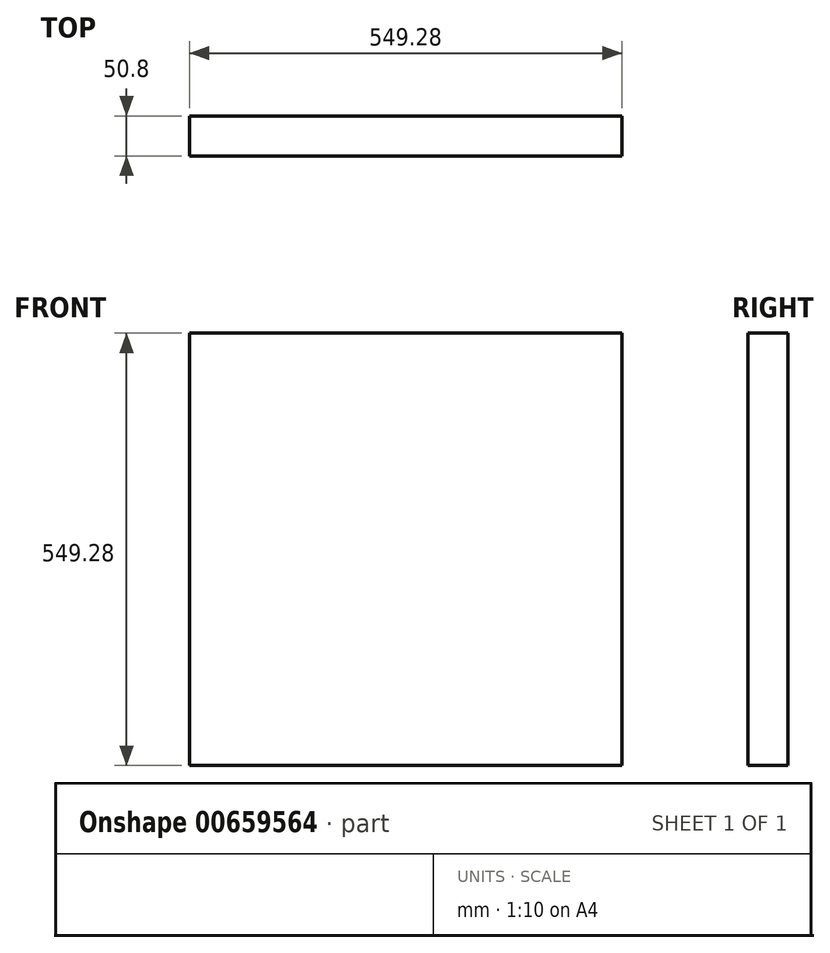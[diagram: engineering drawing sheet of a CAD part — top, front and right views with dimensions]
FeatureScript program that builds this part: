
annotation { "Feature Type Name" : "Feature", "Feature Type Description" : "" }
export const myFeature = defineFeature(function(context is Context, id is Id, definition is map)
    precondition{}
    {
        {
            var Q0;
            Q0=qCreatedBy(makeId("Front.planeOp"),FACE);
            var sketch = newSketch(context, id + "F0", { "sketchPlane" : qUnion([Q0])});
            skLineSegment(sketch, "E0.bottom", {"start": v(274.64, 274.64) * mm, "end": v(-274.64, 274.64) * mm});
            skLineSegment(sketch, "E0.top", {"start": v(274.64, -274.64) * mm, "end": v(-274.64, -274.64) * mm});
            skLineSegment(sketch, "E0.left", {"start": v(274.64, 274.64) * mm, "end": v(274.64, -274.64) * mm});
            skLineSegment(sketch, "E0.right", {"start": v(-274.64, 274.64) * mm, "end": v(-274.64, -274.64) * mm});
            skPoint(sketch, "E0.middle", {"position": v(0, 0) * mm});
            skLineSegment(sketch, "E1", {"start": v(-274.64, 274.64) * mm, "end": v(-273.37, 274.64) * mm, "construction": true});
            skLineSegment(sketch, "E2", {"start": v(-273.37, 274.64) * mm, "end": v(-273.37, 273.37) * mm, "construction": true});
            skPoint(sketch, "E3", {"position": v(-273.37, 273.37) * mm});
            skLineSegment(sketch, "E4.bottom", {"start": v(-273.37, 273.37) * mm, "end": v(-209.87, 273.37) * mm});
            skLineSegment(sketch, "E4.top", {"start": v(-273.37, 209.87) * mm, "end": v(-209.87, 209.87) * mm});
            skLineSegment(sketch, "E4.left", {"start": v(-273.37, 273.37) * mm, "end": v(-273.37, 209.87) * mm});
            skLineSegment(sketch, "E4.right", {"start": v(-209.87, 273.37) * mm, "end": v(-209.87, 209.87) * mm});
            skLineSegment(sketch, "E5", {"start": v(0, 0) * mm, "end": v(0, 20.48) * mm});
            skLineSegment(sketch, "E6", {"start": v(0, 20.48) * mm, "end": v(0, 0) * mm});
            skLineSegment(sketch, "E7", {"start": v(28.9, 0) * mm, "end": v(0, 0) * mm});
            skLineSegment(sketch, "E8.MirrorCS", {"start": v(209.87, 273.37) * mm, "end": v(209.87, 209.87) * mm});
            skLineSegment(sketch, "E9.MirrorCS", {"start": v(273.37, 209.87) * mm, "end": v(209.87, 209.87) * mm});
            skLineSegment(sketch, "E10.MirrorCS", {"start": v(273.37, 273.37) * mm, "end": v(273.37, 209.87) * mm});
            skLineSegment(sketch, "E11.MirrorCS", {"start": v(273.37, 273.37) * mm, "end": v(209.87, 273.37) * mm});
            skLineSegment(sketch, "E12.MirrorCS", {"start": v(-209.87, -273.37) * mm, "end": v(-209.87, -209.87) * mm});
            skLineSegment(sketch, "E13.MirrorCS", {"start": v(-273.37, -209.87) * mm, "end": v(-209.87, -209.87) * mm});
            skLineSegment(sketch, "E14.MirrorCS", {"start": v(-273.37, -273.37) * mm, "end": v(-273.37, -209.87) * mm});
            skLineSegment(sketch, "E15.MirrorCS", {"start": v(-273.37, -273.37) * mm, "end": v(-209.87, -273.37) * mm});
            skLineSegment(sketch, "E16.MirrorCS", {"start": v(273.37, -209.87) * mm, "end": v(209.87, -209.87) * mm});
            skLineSegment(sketch, "E17.MirrorCS", {"start": v(209.87, -273.37) * mm, "end": v(209.87, -209.87) * mm});
            skLineSegment(sketch, "E18.MirrorCS", {"start": v(273.37, -273.37) * mm, "end": v(273.37, -209.87) * mm});
            skLineSegment(sketch, "E19.MirrorCS", {"start": v(273.37, -273.37) * mm, "end": v(209.87, -273.37) * mm});
            skSolve(sketch);
        }
        {
            var Q0;
            Q0=makeQuery(id+"F0.imprint","IMPRINT",FACE,{"disambiguationData":[TD([[makeQuery(id+"F0.imprint","IMPRINT",EDGE,{"derivedFrom":sQuery(id+"F0.wireOp",EDGE,"E0.bottom")}),1.0]])]});
            var Q1;
            Q1=makeQuery(id+"F0.imprint","IMPRINT",FACE,{"disambiguationData":[TD([[makeQuery(id+"F0.imprint","IMPRINT",EDGE,{"derivedFrom":sQuery(id+"F0.wireOp",EDGE,"E8.MirrorCS")}),1.0]])]});
            var Q2;
            Q2=makeQuery(id+"F0.imprint","IMPRINT",FACE,{"disambiguationData":[TD([[makeQuery(id+"F0.imprint","IMPRINT",EDGE,{"derivedFrom":sQuery(id+"F0.wireOp",EDGE,"E4.bottom")}),-1.0]])]});
            var Q3;
            Q3=makeQuery(id+"F0.imprint","IMPRINT",FACE,{"disambiguationData":[TD([[makeQuery(id+"F0.imprint","IMPRINT",EDGE,{"derivedFrom":sQuery(id+"F0.wireOp",EDGE,"E12.MirrorCS")}),1.0]])]});
            var Q4;
            Q4=makeQuery(id+"F0.imprint","IMPRINT",FACE,{"disambiguationData":[TD([[makeQuery(id+"F0.imprint","IMPRINT",EDGE,{"derivedFrom":sQuery(id+"F0.wireOp",EDGE,"E16.MirrorCS")}),1.0]])]});
            extrude(context, id + "F1", {"entities" : qUnion([Q0, Q1, Q2, Q3, Q4]), "depth" : 50.8 * mm});
        }
    });
